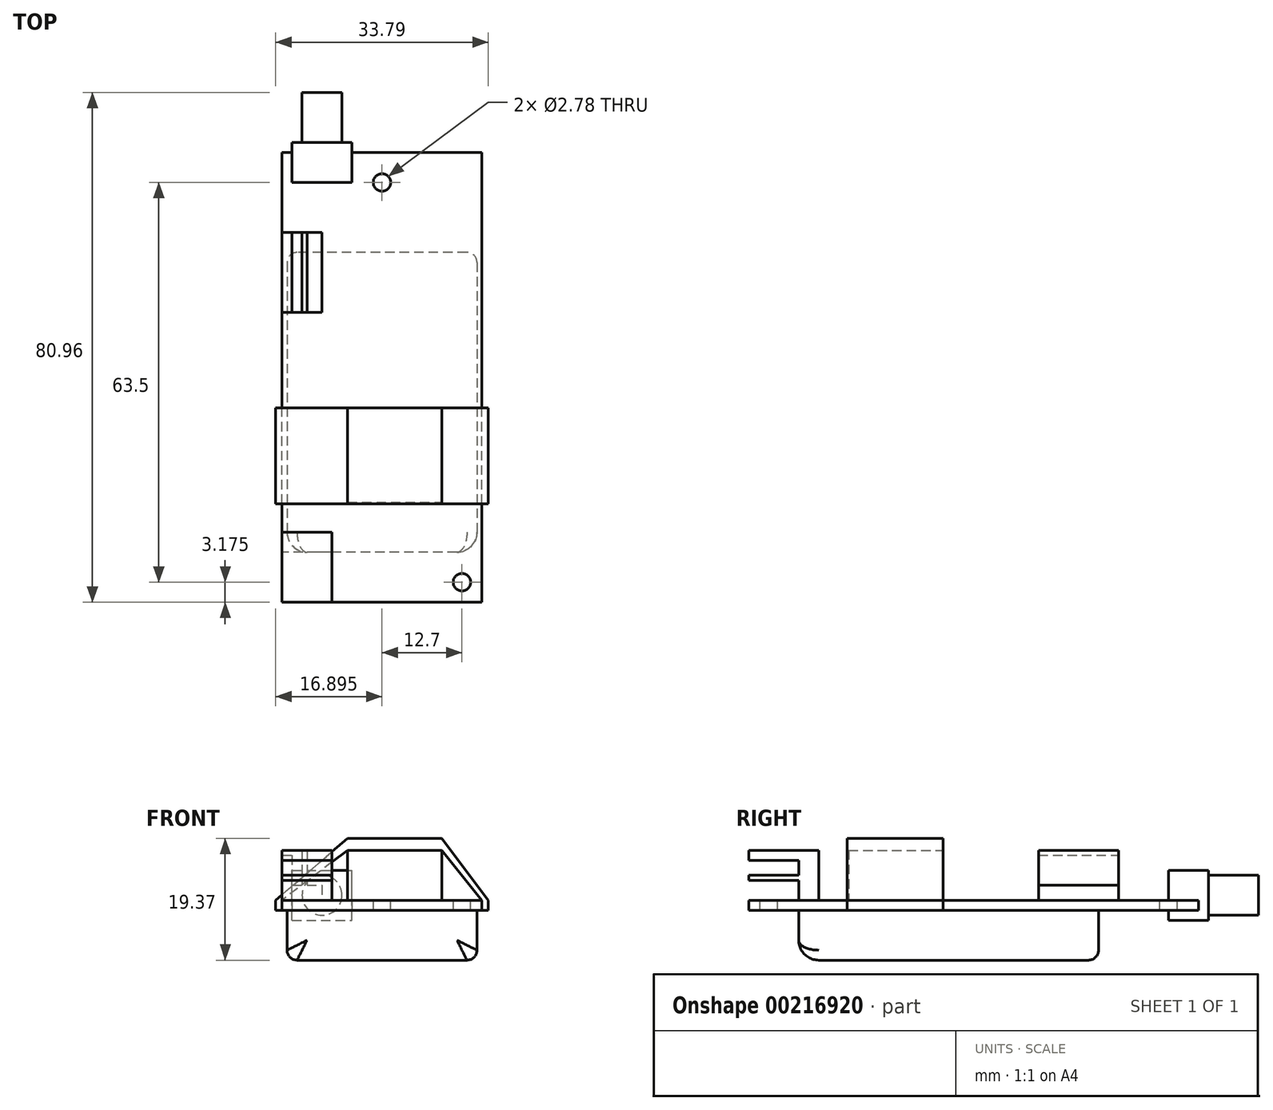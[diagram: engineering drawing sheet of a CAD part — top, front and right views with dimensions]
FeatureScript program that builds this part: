
annotation { "Feature Type Name" : "Feature", "Feature Type Description" : "" }
export const myFeature = defineFeature(function(context is Context, id is Id, definition is map)
    precondition{}
    {
        {
            var Q0;
            Q0=qCreatedBy(makeId("Top.planeOp"),FACE);
            var sketch = newSketch(context, id + "F0", { "sketchPlane" : qUnion([Q0])});
            skLineSegment(sketch, "E0.bottom", {"start": v(0, 0) * mm, "end": v(31.75, 0) * mm});
            skLineSegment(sketch, "E0.top", {"start": v(0, 71.44) * mm, "end": v(31.75, 71.44) * mm});
            skLineSegment(sketch, "E0.left", {"start": v(0, 0) * mm, "end": v(0, 71.44) * mm});
            skLineSegment(sketch, "E0.right", {"start": v(31.75, 0) * mm, "end": v(31.75, 71.44) * mm});
            skSolve(sketch);
        }
        {
            var Q0;
            Q0 = qSketchRegion(id + "F0", true);
            extrude(context, id + "F1", {"entities" : qUnion([Q0]), "depth" : 1.59 * mm});
        }
        {
            var Q0;
            Q0=makeQuery(id+"F1.opExtrude","CAP_FACE",FACE,{"disambiguationData":[OSD([sQuery(id+"F0.wireOp",EDGE,"E0.bottom"),sQuery(id+"F0.wireOp",EDGE,"E0.top"),sQuery(id+"F0.wireOp",EDGE,"E0.left"),sQuery(id+"F0.wireOp",EDGE,"E0.right")])],"isStart":false});
            var sketch = newSketch(context, id + "F2", { "sketchPlane" : qUnion([Q0])});
            skCircle(sketch, "E1", {"center": v(15.88, 66.67) * mm, "radius": 1.39 * mm});
            skCircle(sketch, "E2", {"center": v(28.57, 3.18) * mm, "radius": 1.39 * mm});
            skSolve(sketch);
        }
        {
            var Q0;
            Q0 = qSketchRegion(id + "F2", true);
            extrude(context, id + "F3", {"entities" : qUnion([Q0]), "operationType" : NewBodyOperationType.REMOVE, "oppositeDirection" : true, "depth" : 25.4 * mm});
        }
        {
            var Q0;
            Q0=makeQuery(id+"F1.opExtrude","CAP_FACE",FACE,{"disambiguationData":[OSD([sQuery(id+"F0.wireOp",EDGE,"E0.bottom"),sQuery(id+"F0.wireOp",EDGE,"E0.top"),sQuery(id+"F0.wireOp",EDGE,"E0.left"),sQuery(id+"F0.wireOp",EDGE,"E0.right")])],"isStart":false});
            var sketch = newSketch(context, id + "F4", { "sketchPlane" : qUnion([Q0])});
            skLineSegment(sketch, "E3.bottom", {"start": v(0, 11.11) * mm, "end": v(7.94, 11.11) * mm});
            skLineSegment(sketch, "E3.top", {"start": v(0, 0) * mm, "end": v(7.94, 0) * mm});
            skLineSegment(sketch, "E3.left", {"start": v(0, 11.11) * mm, "end": v(0, 0) * mm});
            skLineSegment(sketch, "E3.right", {"start": v(7.94, 11.11) * mm, "end": v(7.94, 0) * mm});
            skSolve(sketch);
        }
        {
            var Q0;
            Q0 = qSketchRegion(id + "F4", true);
            extrude(context, id + "F5", {"entities" : qUnion([Q0]), "operationType" : NewBodyOperationType.ADD, "depth" : 7.94 * mm});
        }
        {
            var Q0;
            Q0=makeQuery(id+"F5.boolean.opBoolean","MERGE",FACE,{"derivedFrom":[makeQuery(id+"F1.opExtrude","SWEPT_FACE",FACE,{"disambiguationData":[OSD([sQuery(id+"F0.wireOp",EDGE,"E0.left")])]}),makeQuery(id+"F5.opExtrude","SWEPT_FACE",FACE,{"disambiguationData":[OSD([sQuery(id+"F4.wireOp",EDGE,"E3.left")])]})]});
            var sketch = newSketch(context, id + "F6", { "sketchPlane" : qUnion([Q0])});
            skLineSegment(sketch, "E4.bottom", {"start": v(0, 7.94) * mm, "end": v(-7.94, 7.94) * mm});
            skLineSegment(sketch, "E4.top", {"start": v(0, 1.59) * mm, "end": v(-7.94, 1.59) * mm});
            skLineSegment(sketch, "E4.left", {"start": v(0, 7.94) * mm, "end": v(0, 1.59) * mm});
            skLineSegment(sketch, "E4.right", {"start": v(-7.94, 7.94) * mm, "end": v(-7.94, 1.59) * mm});
            skLineSegment(sketch, "E5.bottom", {"start": v(-7.94, 5.56) * mm, "end": v(0, 5.56) * mm});
            skLineSegment(sketch, "E5.top", {"start": v(-7.94, 4.76) * mm, "end": v(0, 4.76) * mm});
            skLineSegment(sketch, "E5.left", {"start": v(-7.94, 5.56) * mm, "end": v(-7.94, 4.76) * mm});
            skLineSegment(sketch, "E5.right", {"start": v(0, 5.56) * mm, "end": v(0, 4.76) * mm});
            skSolve(sketch);
        }
        {
            var Q0;
            {var subQ0=sQuery(id+"F6.wireOp",EDGE,"E4.top");Q0=makeQuery(id+"F6.imprint","IMPRINT",FACE,{"disambiguationData":[TD([[makeQuery(id+"F6.imprint","IMPRINT",EDGE,{"derivedFrom":subQ0}),-1.0]])]});}
            var Q1;
            {var subQ0=sQuery(id+"F6.wireOp",EDGE,"E4.bottom");Q1=makeQuery(id+"F6.imprint","IMPRINT",FACE,{"disambiguationData":[TD([[makeQuery(id+"F6.imprint","IMPRINT",EDGE,{"derivedFrom":subQ0}),1.0]])]});}
            extrude(context, id + "F7", {"entities" : qUnion([Q0, Q1]), "operationType" : NewBodyOperationType.REMOVE, "oppositeDirection" : true, "depth" : 25.4 * mm});
        }
        {
            var Q0;
            Q0=makeQuery(id+"F7.boolean.opBoolean","MERGE",FACE,{"derivedFrom":[makeQuery(id+"F1.opExtrude","CAP_FACE",FACE,{"disambiguationData":[OSD([sQuery(id+"F0.wireOp",EDGE,"E0.bottom"),sQuery(id+"F0.wireOp",EDGE,"E0.top"),sQuery(id+"F0.wireOp",EDGE,"E0.left"),sQuery(id+"F0.wireOp",EDGE,"E0.right")])],"isStart":false}),makeQuery(id+"F7.opExtrude","SWEPT_FACE",FACE,{"disambiguationData":[OSD([sQuery(id+"F6.wireOp",EDGE,"E4.top")])]})]});
            var sketch = newSketch(context, id + "F8", { "sketchPlane" : qUnion([Q0])});
            skLineSegment(sketch, "E6.bottom", {"start": v(0, 58.74) * mm, "end": v(6.35, 58.74) * mm});
            skLineSegment(sketch, "E6.top", {"start": v(0, 46.04) * mm, "end": v(6.35, 46.04) * mm});
            skLineSegment(sketch, "E6.left", {"start": v(0, 58.74) * mm, "end": v(0, 46.04) * mm});
            skLineSegment(sketch, "E6.right", {"start": v(6.35, 58.74) * mm, "end": v(6.35, 46.04) * mm});
            skSolve(sketch);
        }
        {
            var Q0;
            Q0 = qSketchRegion(id + "F8", true);
            extrude(context, id + "F9", {"entities" : qUnion([Q0]), "operationType" : NewBodyOperationType.ADD, "depth" : 2.38 * mm});
        }
        {
            var Q0;
            Q0=makeQuery(id+"F9.opExtrude","CAP_FACE",FACE,{"disambiguationData":[OSD([sQuery(id+"F8.wireOp",EDGE,"E6.bottom"),sQuery(id+"F8.wireOp",EDGE,"E6.top"),sQuery(id+"F8.wireOp",EDGE,"E6.left"),sQuery(id+"F8.wireOp",EDGE,"E6.right")])],"isStart":false});
            var sketch = newSketch(context, id + "F10", { "sketchPlane" : qUnion([Q0])});
            skLineSegment(sketch, "E7.bottom", {"start": v(0, 58.74) * mm, "end": v(1.59, 58.74) * mm});
            skLineSegment(sketch, "E7.top", {"start": v(0, 46.04) * mm, "end": v(1.59, 46.04) * mm});
            skLineSegment(sketch, "E7.left", {"start": v(0, 58.74) * mm, "end": v(0, 46.04) * mm});
            skLineSegment(sketch, "E7.right", {"start": v(1.59, 58.74) * mm, "end": v(1.59, 46.04) * mm});
            skSolve(sketch);
        }
        {
            var Q0;
            Q0 = qSketchRegion(id + "F10", true);
            extrude(context, id + "F11", {"entities" : qUnion([Q0]), "operationType" : NewBodyOperationType.ADD, "depth" : 4.76 * mm});
        }
        {
            var Q0;
            Q0=makeQuery(id+"F9.opExtrude","CAP_FACE",FACE,{"disambiguationData":[OSD([sQuery(id+"F8.wireOp",EDGE,"E6.bottom"),sQuery(id+"F8.wireOp",EDGE,"E6.top"),sQuery(id+"F8.wireOp",EDGE,"E6.left"),sQuery(id+"F8.wireOp",EDGE,"E6.right")])],"isStart":false});
            var sketch = newSketch(context, id + "F12", { "sketchPlane" : qUnion([Q0])});
            skLineSegment(sketch, "E8.bottom", {"start": v(3.18, 58.74) * mm, "end": v(3.97, 58.74) * mm});
            skLineSegment(sketch, "E8.top", {"start": v(3.18, 46.04) * mm, "end": v(3.97, 46.04) * mm});
            skLineSegment(sketch, "E8.left", {"start": v(3.18, 58.74) * mm, "end": v(3.18, 46.04) * mm});
            skLineSegment(sketch, "E8.right", {"start": v(3.97, 58.74) * mm, "end": v(3.97, 46.04) * mm});
            skSolve(sketch);
        }
        {
            var Q0;
            Q0 = qSketchRegion(id + "F12", true);
            extrude(context, id + "F13", {"entities" : qUnion([Q0]), "operationType" : NewBodyOperationType.ADD, "depth" : 5.56 * mm});
        }
        {
            var Q0;
            Q0=makeQuery(id+"F1.opExtrude","CAP_FACE",FACE,{"disambiguationData":[OSD([sQuery(id+"F0.wireOp",EDGE,"E0.bottom"),sQuery(id+"F0.wireOp",EDGE,"E0.top"),sQuery(id+"F0.wireOp",EDGE,"E0.left"),sQuery(id+"F0.wireOp",EDGE,"E0.right")])],"isStart":true});
            var sketch = newSketch(context, id + "F14", { "sketchPlane" : qUnion([Q0])});
            skLineSegment(sketch, "E9.bottom", {"start": v(1.59, -66.68) * mm, "end": v(11.11, -66.68) * mm});
            skLineSegment(sketch, "E9.top", {"start": v(1.59, -73.03) * mm, "end": v(11.11, -73.03) * mm});
            skLineSegment(sketch, "E9.left", {"start": v(1.59, -66.68) * mm, "end": v(1.59, -73.03) * mm});
            skLineSegment(sketch, "E9.right", {"start": v(11.11, -66.68) * mm, "end": v(11.11, -73.03) * mm});
            skSolve(sketch);
        }
        {
            var Q0;
            Q0 = qSketchRegion(id + "F14", true);
            extrude(context, id + "F15", {"entities" : qUnion([Q0]), "operationType" : NewBodyOperationType.ADD, "depth" : 1.59 * mm, "hasSecondDirection" : true, "secondDirectionOppositeDirection" : true, "secondDirectionDepth" : 6.35 * mm});
        }
        {
            var Q0;
            Q0=makeQuery(id+"F15.opExtrude","SWEPT_FACE",FACE,{"disambiguationData":[OSD([sQuery(id+"F14.wireOp",EDGE,"E9.top")])]});
            var sketch = newSketch(context, id + "F16", { "sketchPlane" : qUnion([Q0])});
            skCircle(sketch, "E10", {"center": v(-6.35, 2.38) * mm, "radius": 3.18 * mm});
            skSolve(sketch);
        }
        {
            var Q0;
            Q0 = qSketchRegion(id + "F16", true);
            extrude(context, id + "F17", {"entities" : qUnion([Q0]), "operationType" : NewBodyOperationType.ADD, "depth" : 7.94 * mm});
        }
        {
            var Q0;
            Q0=makeQuery(id+"F7.boolean.opBoolean","MERGE",FACE,{"derivedFrom":[makeQuery(id+"F1.opExtrude","CAP_FACE",FACE,{"disambiguationData":[OSD([sQuery(id+"F0.wireOp",EDGE,"E0.bottom"),sQuery(id+"F0.wireOp",EDGE,"E0.top"),sQuery(id+"F0.wireOp",EDGE,"E0.left"),sQuery(id+"F0.wireOp",EDGE,"E0.right")])],"isStart":false}),makeQuery(id+"F7.opExtrude","SWEPT_FACE",FACE,{"disambiguationData":[OSD([sQuery(id+"F6.wireOp",EDGE,"E4.top")])]})]});
            var sketch = newSketch(context, id + "F18", { "sketchPlane" : qUnion([Q0])});
            skLineSegment(sketch, "E11.bottom", {"start": v(10.4, 15.88) * mm, "end": v(25.4, 15.88) * mm});
            skLineSegment(sketch, "E11.top", {"start": v(10.4, 30.88) * mm, "end": v(25.4, 30.88) * mm});
            skLineSegment(sketch, "E11.left", {"start": v(10.4, 15.88) * mm, "end": v(10.4, 30.88) * mm});
            skLineSegment(sketch, "E11.right", {"start": v(25.4, 15.88) * mm, "end": v(25.4, 30.88) * mm});
            skSolve(sketch);
        }
        {
            var Q0;
            Q0 = qSketchRegion(id + "F18", true);
            extrude(context, id + "F19", {"entities" : qUnion([Q0]), "operationType" : NewBodyOperationType.ADD, "depth" : 7.94 * mm});
        }
        {
            var Q0;
            Q0=makeQuery(id+"F1.opExtrude","CAP_FACE",FACE,{"disambiguationData":[OSD([sQuery(id+"F0.wireOp",EDGE,"E0.bottom"),sQuery(id+"F0.wireOp",EDGE,"E0.top"),sQuery(id+"F0.wireOp",EDGE,"E0.left"),sQuery(id+"F0.wireOp",EDGE,"E0.right")])],"isStart":true});
            var sketch = newSketch(context, id + "F20", { "sketchPlane" : qUnion([Q0])});
            skLineSegment(sketch, "E12.bottom", {"start": v(30.96, -55.56) * mm, "end": v(0.8, -55.56) * mm});
            skLineSegment(sketch, "E12.top", {"start": v(30.96, -7.94) * mm, "end": v(0.8, -7.94) * mm});
            skLineSegment(sketch, "E12.left", {"start": v(30.96, -55.56) * mm, "end": v(30.96, -7.94) * mm});
            skLineSegment(sketch, "E12.right", {"start": v(0.8, -55.56) * mm, "end": v(0.8, -7.94) * mm});
            skSolve(sketch);
        }
        {
            var Q0;
            Q0 = qSketchRegion(id + "F20", true);
            extrude(context, id + "F21", {"entities" : qUnion([Q0]), "operationType" : NewBodyOperationType.ADD, "depth" : 7.94 * mm});
        }
        {
            var Q0;
            Q0=makeQuery(id+"F21.opExtrude","CAP_EDGE",EDGE,{"disambiguationData":[OSD([sQuery(id+"F20.wireOp",EDGE,"E12.left")])],"isStart":false});
            var Q1;
            Q1=makeQuery(id+"F21.opExtrude","CAP_EDGE",EDGE,{"disambiguationData":[OSD([sQuery(id+"F20.wireOp",EDGE,"E12.right")])],"isStart":false});
            fillet(context, id + "F22", {"entities" : qUnion([Q0, Q1]), "radius" : 1.59 * mm, "tangentPropagation" : true, "allowEdgeOverflow" : false});
        }
        {
            var Q0;
            Q0=makeQuery(id+"F21.opExtrude","CAP_EDGE",EDGE,{"disambiguationData":[OSD([sQuery(id+"F20.wireOp",EDGE,"E12.top")])],"isStart":false});
            fillet(context, id + "F23", {"entities" : qUnion([Q0]), "radius" : 3.17 * mm, "tangentPropagation" : true, "allowEdgeOverflow" : false});
        }
        {
            var Q0;
            Q0=makeQuery(id+"F21.opExtrude","CAP_EDGE",EDGE,{"disambiguationData":[OSD([sQuery(id+"F20.wireOp",EDGE,"E12.bottom")])],"isStart":false});
            fillet(context, id + "F24", {"entities" : qUnion([Q0]), "radius" : 1.59 * mm, "tangentPropagation" : true, "allowEdgeOverflow" : false});
        }
        {
            var Q0;
            Q0=makeQuery(id+"F19.opExtrude","SWEPT_FACE",FACE,{"disambiguationData":[OSD([sQuery(id+"F18.wireOp",EDGE,"E11.top")])]});
            var sketch = newSketch(context, id + "F25", { "sketchPlane" : qUnion([Q0])});
            skLineSegment(sketch, "E13", {"start": v(-25.4, 11.43) * mm, "end": v(-10.4, 11.43) * mm});
            skLineSegment(sketch, "E14", {"start": v(-10.4, 9.53) * mm, "end": v(-25.4, 9.53) * mm});
            skLineSegment(sketch, "E15", {"start": v(-25.4, 9.52) * mm, "end": v(-31.75, 1.59) * mm});
            skLineSegment(sketch, "E16", {"start": v(-31.75, 1.59) * mm, "end": v(-31.75, 0) * mm});
            skLineSegment(sketch, "E17", {"start": v(-31.75, 0) * mm, "end": v(-32.77, 0) * mm});
            skLineSegment(sketch, "E18", {"start": v(-32.77, 0) * mm, "end": v(-32.77, 1.59) * mm});
            skLineSegment(sketch, "E19", {"start": v(-32.77, 1.59) * mm, "end": v(-25.4, 11.43) * mm});
            skLineSegment(sketch, "E20", {"start": v(-10.4, 9.53) * mm, "end": v(0, 1.59) * mm});
            skLineSegment(sketch, "E21", {"start": v(1.02, 1.59) * mm, "end": v(1.02, 0) * mm});
            skLineSegment(sketch, "E22", {"start": v(1.02, 0) * mm, "end": v(0, 0) * mm});
            skLineSegment(sketch, "E23", {"start": v(0, 0) * mm, "end": v(0, 1.59) * mm});
            skLineSegment(sketch, "E24", {"start": v(1.02, 1.59) * mm, "end": v(-10.4, 11.43) * mm});
            skSolve(sketch);
        }
        {
            var Q0;
            Q0 = qSketchRegion(id + "F25", true);
            extrude(context, id + "F26", {"entities" : qUnion([Q0]), "operationType" : NewBodyOperationType.ADD, "oppositeDirection" : true, "depth" : 15.24 * mm});
        }
    });
